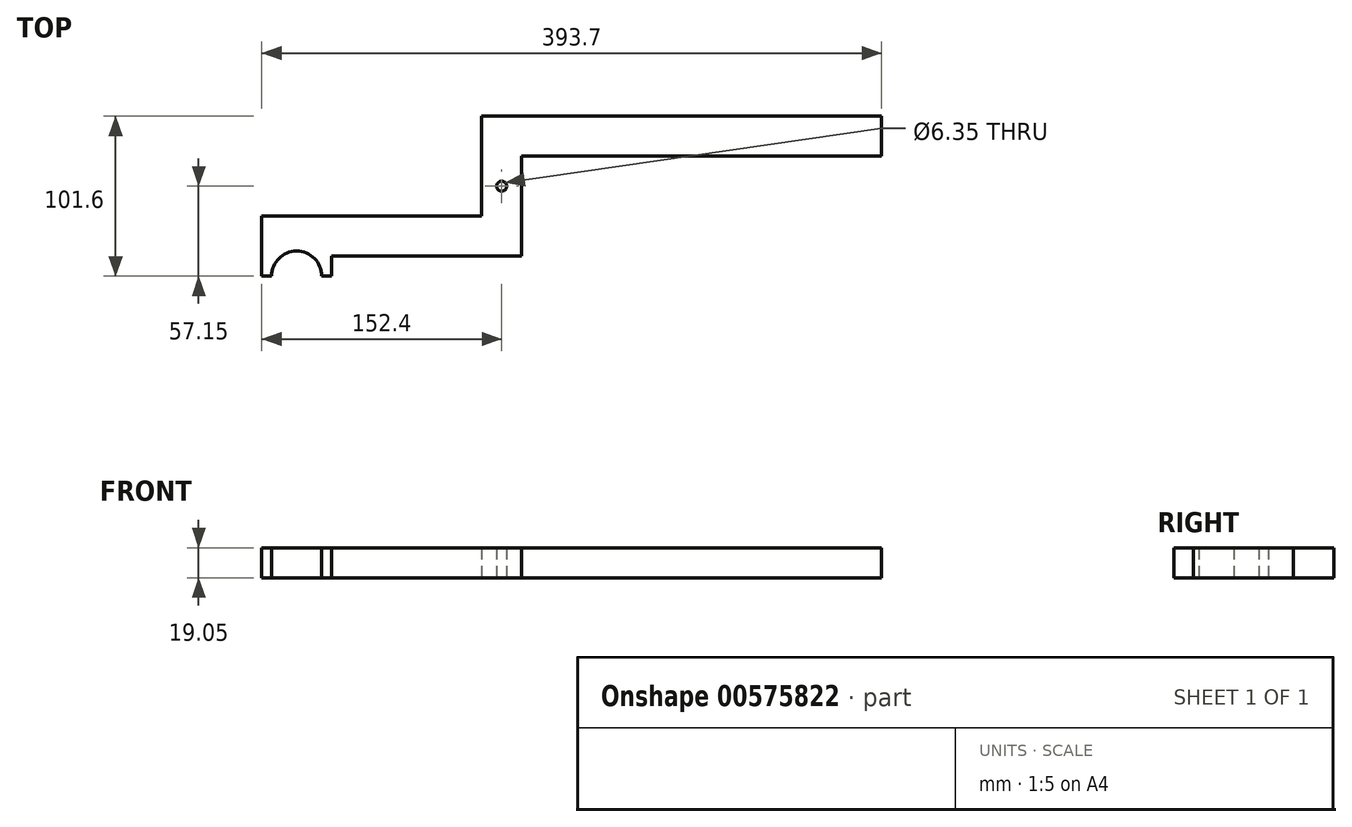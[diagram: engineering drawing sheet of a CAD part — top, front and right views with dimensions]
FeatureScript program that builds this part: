
annotation { "Feature Type Name" : "Feature", "Feature Type Description" : "" }
export const myFeature = defineFeature(function(context is Context, id is Id, definition is map)
    precondition{}
    {
        {
            var Q0;
            Q0=qCreatedBy(makeId("Top.planeOp"),FACE);
            var sketch = newSketch(context, id + "F0", { "sketchPlane" : qUnion([Q0])});
            skLineSegment(sketch, "E0", {"start": v(0, 0) * mm, "end": v(0, 50.8) * mm});
            skLineSegment(sketch, "E1", {"start": v(0, 50.8) * mm, "end": v(254, 50.8) * mm});
            skLineSegment(sketch, "E2", {"start": v(254, 50.8) * mm, "end": v(254, 25.4) * mm});
            skLineSegment(sketch, "E3", {"start": v(254, 25.4) * mm, "end": v(25.4, 25.4) * mm});
            skLineSegment(sketch, "E4", {"start": v(25.4, 25.4) * mm, "end": v(25.4, 0) * mm});
            skLineSegment(sketch, "E5", {"start": v(25.4, 0) * mm, "end": v(25.4, -38.1) * mm});
            skLineSegment(sketch, "E6", {"start": v(0, 0) * mm, "end": v(0, -12.7) * mm});
            skLineSegment(sketch, "E7", {"start": v(0, -12.7) * mm, "end": v(-133.35, -12.7) * mm});
            skLineSegment(sketch, "E8", {"start": v(-133.35, -12.7) * mm, "end": v(-133.35, -50.8) * mm});
            skCircle(sketch, "E9", {"center": v(12.7, 6.35) * mm, "radius": 3.18 * mm});
            skLineSegment(sketch, "E10", {"start": v(25.4, -38.1) * mm, "end": v(-101.6, -38.1) * mm});
            skLineSegment(sketch, "E11", {"start": v(-101.6, -38.1) * mm, "end": v(-101.6, -50.8) * mm});
            skArc(sketch, "E12", {"start": v(-101.6, -50.8) * mm, "mid": v(-117.48, -34.93) * mm, "end": v(-133.35, -50.8) * mm});
            skSolve(sketch);
        }
        {
            var Q0;
            Q0 = qSketchRegion(id + "F0", true);
            extrude(context, id + "F1", {"entities" : qUnion([Q0]), "depth" : 19.05 * mm, "offsetDistance" : 25.4 * mm});
        }
        {
            var Q0;
            Q0=makeQuery(id+"F1.opExtrude","SWEPT_FACE",FACE,{"disambiguationData":[OSD([sQuery(id+"F0.wireOp",EDGE,"E8")])]});
            var sketch = newSketch(context, id + "F2", { "sketchPlane" : qUnion([Q0])});
            skSolve(sketch);
        }
        {
            var Q0;
            Q0 = qSketchRegion(id + "F2", true);
            var Q1;
            {var subQ0=sQuery(id+"F0.wireOp",EDGE,"E8");Q1=makeQuery(id+"F2.imprint","IMPRINT",FACE,{"disambiguationData":[TD([[makeQuery(id+"F2.imprint","IMPRINT",EDGE,{"derivedFrom":makeQuery(id+"F1.opExtrude","CAP_EDGE",EDGE,{"disambiguationData":[OSD([subQ0])],"isStart":true})}),1.0]])]});}
            extrude(context, id + "F3", {"entities" : qUnion([Q0, Q1]), "operationType" : NewBodyOperationType.ADD, "depth" : 6.35 * mm, "offsetDistance" : 25.4 * mm});
        }
        {
            var Q0;
            Q0=makeQuery(id+"F1.opExtrude","SWEPT_FACE",FACE,{"disambiguationData":[OSD([sQuery(id+"F0.wireOp",EDGE,"E11")])]});
            var sketch = newSketch(context, id + "F4", { "sketchPlane" : qUnion([Q0])});
            skSolve(sketch);
        }
        {
            var Q0;
            Q0 = qSketchRegion(id + "F4", true);
            var Q1;
            {var subQ0=sQuery(id+"F0.wireOp",EDGE,"E11");Q1=makeQuery(id+"F4.imprint","IMPRINT",FACE,{"disambiguationData":[TD([[makeQuery(id+"F4.imprint","IMPRINT",EDGE,{"derivedFrom":makeQuery(id+"F1.opExtrude","CAP_EDGE",EDGE,{"disambiguationData":[OSD([subQ0])],"isStart":true})}),-1.0]])]});}
            extrude(context, id + "F5", {"entities" : qUnion([Q0, Q1]), "operationType" : NewBodyOperationType.ADD, "depth" : 6.35 * mm, "offsetDistance" : 25.4 * mm});
        }
    });
